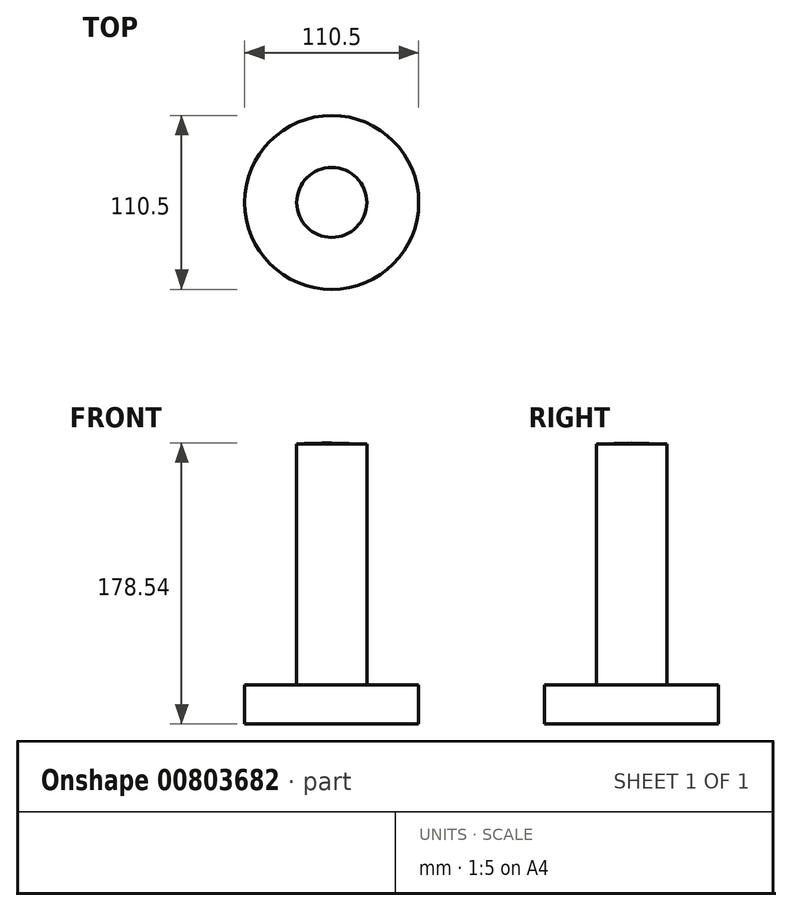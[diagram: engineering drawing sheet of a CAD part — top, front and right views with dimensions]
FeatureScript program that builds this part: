
annotation { "Feature Type Name" : "Feature", "Feature Type Description" : "" }
export const myFeature = defineFeature(function(context is Context, id is Id, definition is map)
    precondition{}
    {
        {
            var Q0;
            Q0=qCreatedBy(makeId("Front.planeOp"),FACE);
            var sketch = newSketch(context, id + "F0", { "sketchPlane" : qUnion([Q0])});
            skLineSegment(sketch, "E0", {"start": v(203.59, 15.91) * mm, "end": v(203.59, -162.63) * mm});
            skLineSegment(sketch, "E1", {"start": v(203.59, -162.63) * mm, "end": v(258.84, -162.63) * mm});
            skLineSegment(sketch, "E2", {"start": v(258.84, -162.63) * mm, "end": v(258.84, -137.7) * mm});
            skLineSegment(sketch, "E3", {"start": v(258.84, -137.7) * mm, "end": v(225.82, -137.7) * mm});
            skLineSegment(sketch, "E4", {"start": v(225.82, -137.7) * mm, "end": v(225.82, 15.28) * mm});
            skLineSegment(sketch, "E5", {"start": v(225.82, 15.28) * mm, "end": v(203.59, 15.91) * mm});
            skSolve(sketch);
        }
        {
            var Q0;
            Q0=makeQuery(id+"F0.imprint","IMPRINT",FACE,{"disambiguationData":[TD([[makeQuery(id+"F0.imprint","IMPRINT",EDGE,{"derivedFrom":sQuery(id+"F0.wireOp",EDGE,"E0")}),1.0]])]});
            var Q1;
            Q1=sQuery(id+"F0.wireOp",EDGE,"E0");
            revolve(context, id + "F1", {"surfaceOperationType" : NewSurfaceOperationType.NEW, "entities" : qUnion([Q0]), "axis" : qUnion([Q1]), "revolveType" : RevolveType.FULL});
        }
    });
